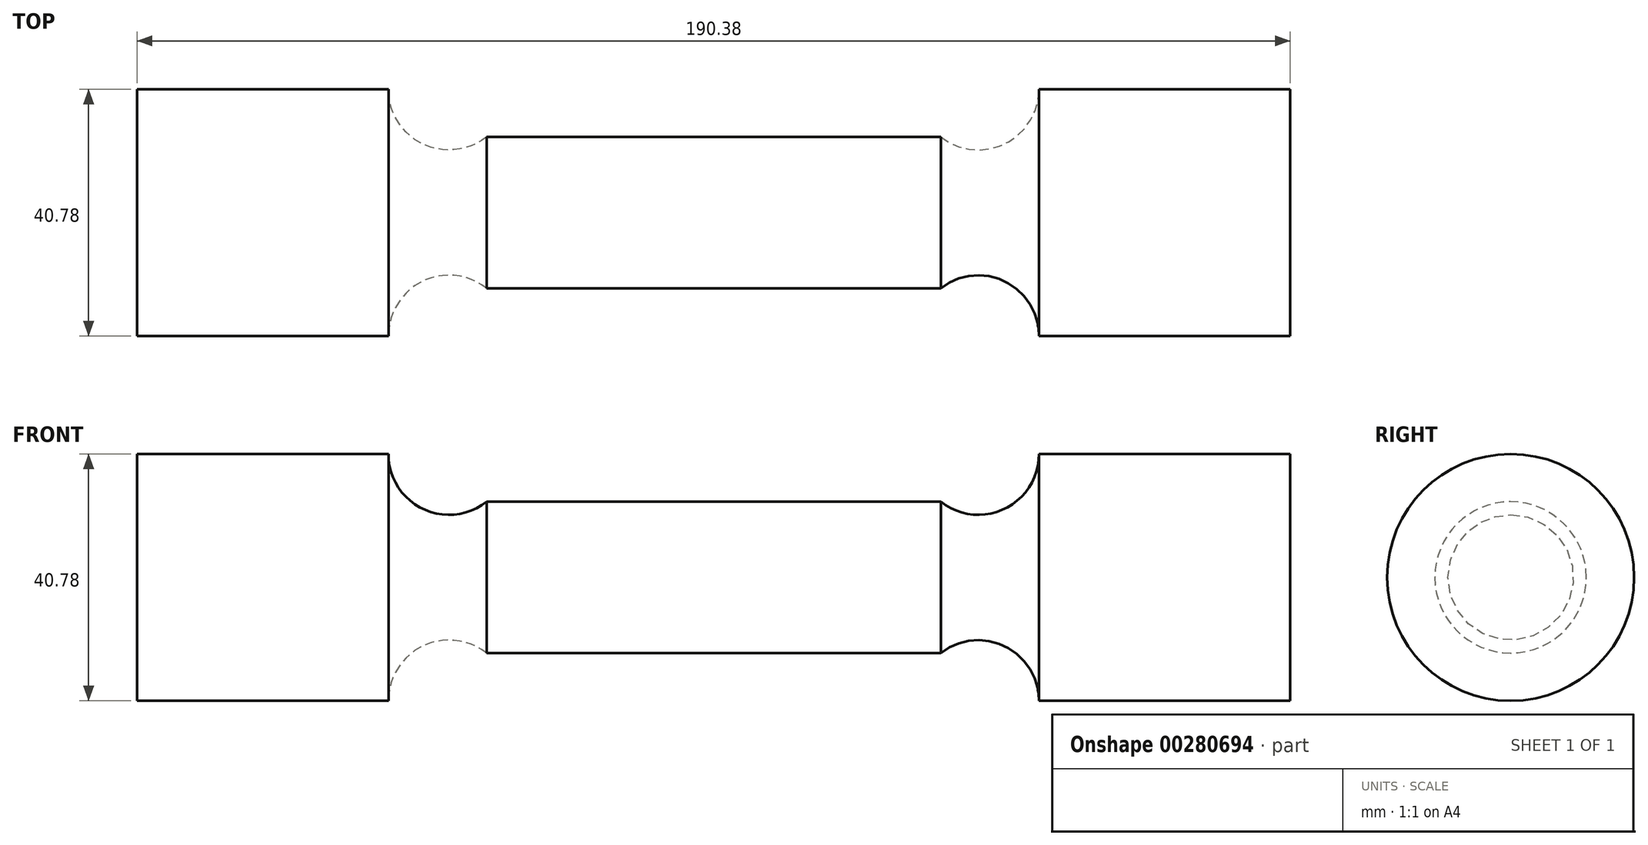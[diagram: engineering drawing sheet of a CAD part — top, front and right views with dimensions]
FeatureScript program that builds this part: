
annotation { "Feature Type Name" : "Feature", "Feature Type Description" : "" }
export const myFeature = defineFeature(function(context is Context, id is Id, definition is map)
    precondition{}
    {
        {
            var Q0;
            Q0=qCreatedBy(makeId("Front.planeOp"),FACE);
            var sketch = newSketch(context, id + "F0", { "sketchPlane" : qUnion([Q0])});
            skLineSegment(sketch, "E0", {"start": v(0, 12.5) * mm, "end": v(37.5, 12.5) * mm});
            skArc(sketch, "E1", {"start": v(37.5, 12.5) * mm, "mid": v(48.07, 11.36) * mm, "end": v(53.7, 20.39) * mm});
            skLineSegment(sketch, "E2", {"start": v(53.7, 20.39) * mm, "end": v(95.2, 20.39) * mm});
            skLineSegment(sketch, "E3", {"start": v(95.2, 20.39) * mm, "end": v(95.2, 0) * mm});
            skLineSegment(sketch, "E4.MirrorCS", {"start": v(0, 12.5) * mm, "end": v(-37.5, 12.5) * mm});
            skLineSegment(sketch, "E5.MirrorCS", {"start": v(-95.2, 20.39) * mm, "end": v(-95.2, 0) * mm});
            skLineSegment(sketch, "E6.MirrorCS", {"start": v(-53.7, 20.39) * mm, "end": v(-95.2, 20.39) * mm});
            skArc(sketch, "E7.MirrorCS", {"start": v(-37.5, 12.5) * mm, "mid": v(-48.07, 11.36) * mm, "end": v(-53.7, 20.39) * mm});
            skLineSegment(sketch, "E8", {"start": v(-95.2, 0) * mm, "end": v(95.2, 0) * mm});
            skSolve(sketch);
        }
        {
            var Q0;
            Q0=makeQuery(id+"F0.imprint","IMPRINT",FACE,{"disambiguationData":[TD([[makeQuery(id+"F0.imprint","IMPRINT",EDGE,{"derivedFrom":sQuery(id+"F0.wireOp",EDGE,"E0")}),-1.0]])]});
            var Q1;
            Q1=sQuery(id+"F0.wireOp",EDGE,"E8");
            revolve(context, id + "F1", {"entities" : qUnion([Q0]), "axis" : qUnion([Q1]), "revolveType" : RevolveType.FULL});
        }
    });
